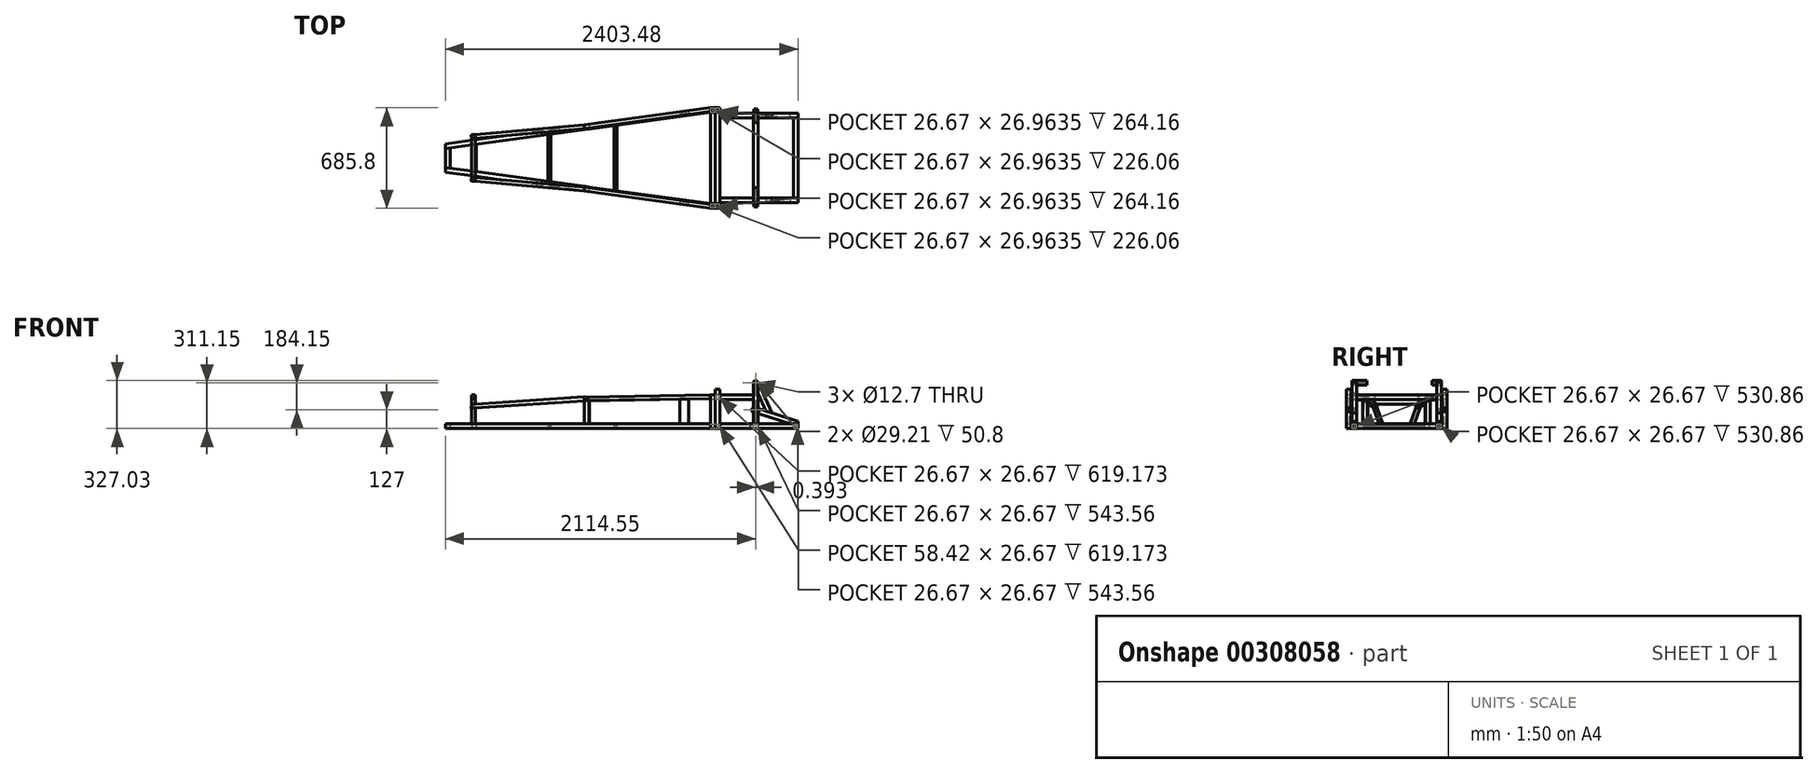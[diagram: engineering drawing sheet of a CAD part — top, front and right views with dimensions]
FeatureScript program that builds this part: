
annotation { "Feature Type Name" : "Feature", "Feature Type Description" : "" }
export const myFeature = defineFeature(function(context is Context, id is Id, definition is map)
    precondition{}
    {
        {
            var Q0;
            Q0=qCreatedBy(makeId("Top.planeOp"),FACE);
            var sketch = newSketch(context, id + "F0", { "sketchPlane" : qUnion([Q0])});
            skLineSegment(sketch, "E0.left", {"start": v(1201.74, -304.8) * mm, "end": v(1201.74, 304.8) * mm});
            skPoint(sketch, "E0.middle", {"position": v(0, 0) * mm});
            skLineSegment(sketch, "E1.0", {"start": v(636.59, -342.9) * mm, "end": v(636.59, -310.86) * mm});
            skLineSegment(sketch, "E2.0", {"start": v(668.34, -342.9) * mm, "end": v(668.34, 342.9) * mm});
            skLineSegment(sketch, "E3", {"start": v(604.84, 342.9) * mm, "end": v(604.84, -342.9) * mm});
            skLineSegment(sketch, "E4", {"start": v(604.84, 342.9) * mm, "end": v(668.34, 342.9) * mm});
            skLineSegment(sketch, "E5.trimOffspring", {"start": v(-1169.99, 0) * mm, "end": v(-1023.94, 0) * mm, "construction": true});
            skLineSegment(sketch, "E6.trimOffspring", {"start": v(668.34, 0) * mm, "end": v(1201.74, 0) * mm, "construction": true});
            skLineSegment(sketch, "E7", {"start": v(604.84, -342.9) * mm, "end": v(668.34, -342.9) * mm});
            skLineSegment(sketch, "E8.0", {"start": v(668.34, -304.8) * mm, "end": v(1201.74, -304.8) * mm});
            skLineSegment(sketch, "E9.0", {"start": v(668.34, 304.8) * mm, "end": v(1201.74, 304.8) * mm});
            skLineSegment(sketch, "E10.0", {"start": v(668.34, 273.05) * mm, "end": v(1201.74, 273.05) * mm});
            skLineSegment(sketch, "E11.0", {"start": v(668.34, -273.05) * mm, "end": v(1201.74, -273.05) * mm});
            skLineSegment(sketch, "E12.0", {"start": v(1169.99, -273.05) * mm, "end": v(1169.99, 273.05) * mm});
            skLineSegment(sketch, "E13.0", {"start": v(-1169.99, -68.98) * mm, "end": v(-1169.99, 68.98) * mm});
            skLineSegment(sketch, "E14", {"start": v(-1023.94, 0) * mm, "end": v(604.84, 0) * mm, "construction": true});
            skLineSegment(sketch, "E15", {"start": v(-1023.94, -88.89) * mm, "end": v(-1023.94, 88.89) * mm});
            skLineSegment(sketch, "E16", {"start": v(604.84, 342.9) * mm, "end": v(-1201.74, 96.7) * mm});
            skLineSegment(sketch, "E17", {"start": v(-1201.74, -96.7) * mm, "end": v(-1201.74, -64.66) * mm});
            skLineSegment(sketch, "E18.0", {"start": v(604.84, 310.86) * mm, "end": v(-1201.74, 64.66) * mm});
            skLineSegment(sketch, "E19.MirrorCS", {"start": v(604.84, -310.86) * mm, "end": v(-1201.74, -64.66) * mm});
            skLineSegment(sketch, "E20.MirrorCS", {"start": v(604.84, -342.9) * mm, "end": v(-1201.74, -96.7) * mm});
            skLineSegment(sketch, "E21.0", {"start": v(-992.19, -93.21) * mm, "end": v(-992.19, 93.21) * mm});
            skLineSegment(sketch, "E22.trimOffspring", {"start": v(-1201.74, 64.66) * mm, "end": v(-1201.74, 96.7) * mm});
            skLineSegment(sketch, "E23", {"start": v(-1201.74, -64.66) * mm, "end": v(-1201.74, 64.66) * mm});
            skLineSegment(sketch, "E24.0", {"start": v(-503.24, -159.85) * mm, "end": v(-503.24, 159.85) * mm});
            skLineSegment(sketch, "E25.0", {"start": v(-484.19, -162.44) * mm, "end": v(-484.19, 162.44) * mm});
            skLineSegment(sketch, "E26", {"start": v(604.84, -310.86) * mm, "end": v(668.34, -310.86) * mm});
            skLineSegment(sketch, "E27", {"start": v(604.84, 310.86) * mm, "end": v(668.34, 310.86) * mm});
            skLineSegment(sketch, "E28", {"start": v(636.59, 310.86) * mm, "end": v(636.59, 342.9) * mm});
            skSolve(sketch);
        }
        {
            var Q0;
            {var subQ5=sQuery(id+"F0.wireOp",EDGE,"E16");Q0=makeQuery(id+"F0.imprint","IMPRINT",FACE,{"disambiguationData":[TD([[makeQuery(id+"F0.imprint","IMPRINT",EDGE,{"derivedFrom":subQ5}),1.0]])]});}
            var Q1;
            {var subQ6=sQuery(id+"F0.wireOp",EDGE,"E17");Q1=makeQuery(id+"F0.imprint","IMPRINT",FACE,{"disambiguationData":[TD([[makeQuery(id+"F0.imprint","IMPRINT",EDGE,{"derivedFrom":subQ6}),-1.0]])]});}
            extrude(context, id + "F1", {"entities" : qUnion([Q0, Q1]), "depth" : 31.75 * mm});
        }
        {
            var Q0;
            {var subQ0=sQuery(id+"F0.wireOp",EDGE,"E15");Q0=makeQuery(id+"F0.imprint","IMPRINT",FACE,{"disambiguationData":[TD([[makeQuery(id+"F0.imprint","IMPRINT",EDGE,{"derivedFrom":subQ0}),-1.0]])]});}
            var Q1;
            {var subQ0=sQuery(id+"F0.wireOp",EDGE,"E13.0");Q1=makeQuery(id+"F0.imprint","IMPRINT",FACE,{"disambiguationData":[TD([[makeQuery(id+"F0.imprint","IMPRINT",EDGE,{"derivedFrom":subQ0}),1.0]])]});}
            extrude(context, id + "F2", {"entities" : qUnion([Q0, Q1]), "depth" : 31.75 * mm});
        }
        {
            var Q0;
            {var subQ0=sQuery(id+"F0.wireOp",EDGE,"E24.0");Q0=makeQuery(id+"F0.imprint","IMPRINT",FACE,{"disambiguationData":[TD([[makeQuery(id+"F0.imprint","IMPRINT",EDGE,{"derivedFrom":subQ0}),-1.0]])]});}
            extrude(context, id + "F3", {"entities" : qUnion([Q0]), "depth" : 19.05 * mm});
        }
        {
            var Q0;
            {var subQ0=sQuery(id+"F0.wireOp",EDGE,"E2.0");var subQ4=makeQuery(id+"F0.imprint","INTERSECT",VERTEX,{"derivedFrom":[subQ0,sQuery(id+"F0.wireOp",EDGE,"E8.0")]});Q0=makeQuery(id+"F0.imprint","IMPRINT",FACE,{"disambiguationData":[TD([[makeQuery(id+"F0.imprint","IMPRINT",EDGE,{"disambiguationData":[TD([[subQ4,1.0]])],"derivedFrom":subQ0}),1.0]])]});}
            extrude(context, id + "F4", {"entities" : qUnion([Q0]), "depth" : 31.75 * mm});
        }
        {
            var Q0;
            {var subQ5=sQuery(id+"F0.wireOp",EDGE,"E28");Q0=makeQuery(id+"F0.imprint","IMPRINT",FACE,{"disambiguationData":[TD([[makeQuery(id+"F0.imprint","IMPRINT",EDGE,{"derivedFrom":subQ5}),1.0]])]});}
            extrude(context, id + "F5", {"entities" : qUnion([Q0]), "depth" : 228.6 * mm});
        }
        {
            var Q0;
            {var subQ0=sQuery(id+"F0.wireOp",EDGE,"E1.0");Q0=makeQuery(id+"F0.imprint","IMPRINT",FACE,{"disambiguationData":[TD([[makeQuery(id+"F0.imprint","IMPRINT",EDGE,{"derivedFrom":subQ0}),1.0]])]});}
            extrude(context, id + "F6", {"entities" : qUnion([Q0]), "depth" : 228.6 * mm});
        }
        {
            var Q0;
            {var subQ5=sQuery(id+"F0.wireOp",EDGE,"E28");Q0=makeQuery(id+"F0.imprint","IMPRINT",FACE,{"disambiguationData":[TD([[makeQuery(id+"F0.imprint","IMPRINT",EDGE,{"derivedFrom":subQ5}),-1.0]])]});}
            extrude(context, id + "F7", {"entities" : qUnion([Q0]), "depth" : 266.7 * mm});
        }
        {
            var Q0;
            {var subQ0=sQuery(id+"F0.wireOp",EDGE,"E1.0");Q0=makeQuery(id+"F0.imprint","IMPRINT",FACE,{"disambiguationData":[TD([[makeQuery(id+"F0.imprint","IMPRINT",EDGE,{"derivedFrom":subQ0}),-1.0]])]});}
            extrude(context, id + "F8", {"entities" : qUnion([Q0]), "depth" : 266.7 * mm});
        }
        {
            var Q0;
            {var subQ5=sQuery(id+"F0.wireOp",EDGE,"E12.0");Q0=makeQuery(id+"F0.imprint","IMPRINT",FACE,{"disambiguationData":[TD([[makeQuery(id+"F0.imprint","IMPRINT",EDGE,{"derivedFrom":subQ5}),-1.0]])]});}
            extrude(context, id + "F9", {"entities" : qUnion([Q0]), "depth" : 31.75 * mm});
        }
        {
            var Q0;
            {var subQ4=sQuery(id+"F0.wireOp",EDGE,"E9.0");Q0=makeQuery(id+"F0.imprint","IMPRINT",FACE,{"disambiguationData":[TD([[makeQuery(id+"F0.imprint","IMPRINT",EDGE,{"derivedFrom":subQ4}),-1.0]])]});}
            var Q1;
            {var subQ4=sQuery(id+"F0.wireOp",EDGE,"E8.0");Q1=makeQuery(id+"F0.imprint","IMPRINT",FACE,{"disambiguationData":[TD([[makeQuery(id+"F0.imprint","IMPRINT",EDGE,{"derivedFrom":subQ4}),1.0]])]});}
            extrude(context, id + "F10", {"entities" : qUnion([Q0, Q1]), "depth" : 31.75 * mm});
        }
        {
            var Q0;
            {var subQ0=sQuery(id+"F0.wireOp",EDGE,"E19.MirrorCS");Q0=makeQuery(id+"F2.opExtrude","SWEPT_FACE",FACE,{"disambiguationData":[OSD([subQ0]),TDD([makeQuery(id+"F0.imprint","IMPRINT",EDGE,{"disambiguationData":[TD([[makeQuery(id+"F0.imprint","INTERSECT",VERTEX,{"derivedFrom":[sQuery(id+"F0.wireOp",EDGE,"E13.0"),subQ0]}),-1.0]])],"derivedFrom":subQ0})])]});}
            var Q1;
            {var subQ0=sQuery(id+"F0.wireOp",EDGE,"E19.MirrorCS");Q1=makeQuery(id+"F2.opExtrude","SWEPT_FACE",FACE,{"disambiguationData":[OSD([subQ0]),TDD([makeQuery(id+"F0.imprint","IMPRINT",EDGE,{"disambiguationData":[TD([[makeQuery(id+"F0.imprint","INTERSECT",VERTEX,{"derivedFrom":[sQuery(id+"F0.wireOp",EDGE,"E15"),subQ0]}),1.0]])],"derivedFrom":subQ0})])]});}
            var Q2;
            Q2=makeQuery(id+"F3.opExtrude","SWEPT_FACE",FACE,{"disambiguationData":[OSD([sQuery(id+"F0.wireOp",EDGE,"E19.MirrorCS")])]});
            shell(context, id + "F11", {"entities" : qUnion([Q0, Q1, Q2]), "thickness" : 2.54 * mm});
        }
        {
            var Q0;
            Q0=makeQuery(id+"F1.opExtrude","SWEPT_FACE",FACE,{"disambiguationData":[OSD([sQuery(id+"F0.wireOp",EDGE,"E22.trimOffspring")])]});
            var Q1;
            Q1=makeQuery(id+"F1.opExtrude","SWEPT_FACE",FACE,{"disambiguationData":[OSD([sQuery(id+"F0.wireOp",EDGE,"E17")])]});
            var Q2;
            Q2=makeQuery(id+"F6.opExtrude","CAP_FACE",FACE,{"disambiguationData":[OSD([sQuery(id+"F0.wireOp",EDGE,"E1.0"),sQuery(id+"F0.wireOp",EDGE,"E3"),sQuery(id+"F0.wireOp",EDGE,"E7"),sQuery(id+"F0.wireOp",EDGE,"E26")])],"isStart":false});
            var Q3;
            Q3=makeQuery(id+"F8.opExtrude","CAP_FACE",FACE,{"disambiguationData":[OSD([sQuery(id+"F0.wireOp",EDGE,"E1.0"),sQuery(id+"F0.wireOp",EDGE,"E2.0"),sQuery(id+"F0.wireOp",EDGE,"E7"),sQuery(id+"F0.wireOp",EDGE,"E26")])],"isStart":false});
            var Q4;
            Q4=makeQuery(id+"F5.opExtrude","CAP_FACE",FACE,{"disambiguationData":[OSD([sQuery(id+"F0.wireOp",EDGE,"E3"),sQuery(id+"F0.wireOp",EDGE,"E4"),sQuery(id+"F0.wireOp",EDGE,"E27"),sQuery(id+"F0.wireOp",EDGE,"E28")])],"isStart":false});
            var Q5;
            Q5=makeQuery(id+"F7.opExtrude","CAP_FACE",FACE,{"disambiguationData":[OSD([sQuery(id+"F0.wireOp",EDGE,"E2.0"),sQuery(id+"F0.wireOp",EDGE,"E4"),sQuery(id+"F0.wireOp",EDGE,"E27"),sQuery(id+"F0.wireOp",EDGE,"E28")])],"isStart":false});
            var Q6;
            {var subQ0=sQuery(id+"F0.wireOp",EDGE,"E0.left");Q6=makeQuery(id+"F10.opExtrude","SWEPT_FACE",FACE,{"disambiguationData":[OSD([subQ0]),TDD([makeQuery(id+"F0.imprint","IMPRINT",EDGE,{"disambiguationData":[TD([[makeQuery(id+"F0.imprint","INTERSECT",VERTEX,{"derivedFrom":[subQ0,sQuery(id+"F0.wireOp",EDGE,"E8.0")]}),-1.0]])],"derivedFrom":subQ0})])]});}
            var Q7;
            {var subQ0=sQuery(id+"F0.wireOp",EDGE,"E0.left");Q7=makeQuery(id+"F10.opExtrude","SWEPT_FACE",FACE,{"disambiguationData":[OSD([subQ0]),TDD([makeQuery(id+"F0.imprint","IMPRINT",EDGE,{"disambiguationData":[TD([[makeQuery(id+"F0.imprint","INTERSECT",VERTEX,{"derivedFrom":[subQ0,sQuery(id+"F0.wireOp",EDGE,"E9.0")]}),1.0]])],"derivedFrom":subQ0})])]});}
            shell(context, id + "F12", {"entities" : qUnion([Q0, Q1, Q2, Q3, Q4, Q5, Q6, Q7]), "thickness" : 2.54 * mm});
        }
        {
            var Q0;
            Q0=makeQuery(id+"F4.opExtrude","SWEPT_FACE",FACE,{"disambiguationData":[OSD([sQuery(id+"F0.wireOp",EDGE,"E26")])]});
            shell(context, id + "F13", {"entities" : qUnion([Q0]), "thickness" : 2.54 * mm});
        }
        {
            var Q0;
            Q0=makeQuery(id+"F9.opExtrude","SWEPT_FACE",FACE,{"disambiguationData":[OSD([sQuery(id+"F0.wireOp",EDGE,"E11.0")])]});
            shell(context, id + "F14", {"entities" : qUnion([Q0]), "thickness" : 2.54 * mm});
        }
        {
            var Q0;
            Q0=makeQuery(id+"F5.opExtrude","SWEPT_FACE",FACE,{"disambiguationData":[OSD([sQuery(id+"F0.wireOp",EDGE,"E27")])]});
            var sketch = newSketch(context, id + "F15", { "sketchPlane" : qUnion([Q0])});
            skLineSegment(sketch, "E29.bottom", {"start": v(604.84, 228.6) * mm, "end": v(636.59, 228.6) * mm});
            skLineSegment(sketch, "E29.top", {"start": v(604.84, 196.85) * mm, "end": v(636.59, 196.85) * mm});
            skLineSegment(sketch, "E29.left", {"start": v(604.84, 228.6) * mm, "end": v(604.84, 196.85) * mm});
            skLineSegment(sketch, "E29.right", {"start": v(636.59, 228.6) * mm, "end": v(636.59, 196.85) * mm});
            skSolve(sketch);
        }
        {
            var Q0;
            Q0 = qSketchRegion(id + "F15", true);
            extrude(context, id + "F16", {"entities" : qUnion([Q0]), "endBound" : BoundingType.UP_TO_NEXT, "depth" : 25.4 * mm});
        }
        {
            var Q0;
            Q0=makeQuery(id+"F7.opExtrude","SWEPT_FACE",FACE,{"disambiguationData":[OSD([sQuery(id+"F0.wireOp",EDGE,"E27")])]});
            var sketch = newSketch(context, id + "F17", { "sketchPlane" : qUnion([Q0])});
            skLineSegment(sketch, "E30.bottom", {"start": v(636.59, 228.6) * mm, "end": v(668.34, 228.6) * mm});
            skLineSegment(sketch, "E30.top", {"start": v(636.59, 196.85) * mm, "end": v(668.34, 196.85) * mm});
            skLineSegment(sketch, "E30.left", {"start": v(636.59, 228.6) * mm, "end": v(636.59, 196.85) * mm});
            skLineSegment(sketch, "E30.right", {"start": v(668.34, 228.6) * mm, "end": v(668.34, 196.85) * mm});
            skSolve(sketch);
        }
        {
            var Q0;
            Q0 = qSketchRegion(id + "F17", true);
            extrude(context, id + "F18", {"entities" : qUnion([Q0]), "endBound" : BoundingType.UP_TO_NEXT, "depth" : 25.4 * mm});
        }
        {
            var Q0;
            Q0=makeQuery(id+"F18.opExtrude","CAP_FACE",FACE,{"disambiguationData":[OSD([sQuery(id+"F17.wireOp",EDGE,"E30.bottom"),sQuery(id+"F17.wireOp",EDGE,"E30.top"),sQuery(id+"F17.wireOp",EDGE,"E30.left"),sQuery(id+"F17.wireOp",EDGE,"E30.right")])],"isStart":false});
            shell(context, id + "F19", {"entities" : qUnion([Q0]), "thickness" : 2.54 * mm});
        }
        {
            var Q0;
            Q0=makeQuery(id+"F10.opExtrude","CAP_FACE",FACE,{"disambiguationData":[OSD([sQuery(id+"F0.wireOp",EDGE,"E0.left"),sQuery(id+"F0.wireOp",EDGE,"E2.0"),sQuery(id+"F0.wireOp",EDGE,"E8.0"),sQuery(id+"F0.wireOp",EDGE,"E11.0")])],"isStart":false});
            var sketch = newSketch(context, id + "F20", { "sketchPlane" : qUnion([Q0])});
            skLineSegment(sketch, "E31.bottom", {"start": v(896.94, -273.05) * mm, "end": v(928.69, -273.05) * mm});
            skLineSegment(sketch, "E31.top", {"start": v(896.94, -304.8) * mm, "end": v(928.69, -304.8) * mm});
            skLineSegment(sketch, "E31.left", {"start": v(896.94, -273.05) * mm, "end": v(896.94, -304.8) * mm});
            skLineSegment(sketch, "E31.right", {"start": v(928.69, -273.05) * mm, "end": v(928.69, -304.8) * mm});
            skSolve(sketch);
        }
        {
            var Q0;
            Q0 = qSketchRegion(id + "F20", true);
            extrude(context, id + "F21", {"entities" : qUnion([Q0]), "depth" : 279.4 * mm});
        }
        {
            var Q0;
            Q0=makeQuery(id+"F21.opExtrude","SWEPT_FACE",FACE,{"disambiguationData":[OSD([sQuery(id+"F20.wireOp",EDGE,"E31.left")])]});
            var sketch = newSketch(context, id + "F22", { "sketchPlane" : qUnion([Q0])});
            skLineSegment(sketch, "E32.bottom", {"start": v(273.05, 228.6) * mm, "end": v(304.8, 228.6) * mm});
            skLineSegment(sketch, "E32.top", {"start": v(273.05, 196.85) * mm, "end": v(304.8, 196.85) * mm});
            skLineSegment(sketch, "E32.left", {"start": v(273.05, 228.6) * mm, "end": v(273.05, 196.85) * mm});
            skLineSegment(sketch, "E32.right", {"start": v(304.8, 228.6) * mm, "end": v(304.8, 196.85) * mm});
            skSolve(sketch);
        }
        {
            var Q0;
            Q0 = qSketchRegion(id + "F22", true);
            extrude(context, id + "F23", {"entities" : qUnion([Q0]), "endBound" : BoundingType.UP_TO_NEXT, "depth" : 25.4 * mm});
        }
        {
            var Q0;
            Q0=makeQuery(id+"F21.opExtrude","SWEPT_FACE",FACE,{"disambiguationData":[OSD([sQuery(id+"F20.wireOp",EDGE,"E31.top")])]});
            var sketch = newSketch(context, id + "F24", { "sketchPlane" : qUnion([Q0])});
            skLineSegment(sketch, "E33", {"start": v(896.94, 311.15) * mm, "end": v(928.69, 311.15) * mm});
            skCircle(sketch, "E34", {"center": v(912.81, 311.15) * mm, "radius": 15.88 * mm});
            skSolve(sketch);
        }
        {
            var Q0;
            Q0 = qSketchRegion(id + "F24", true);
            extrude(context, id + "F25", {"entities" : qUnion([Q0]), "operationType" : NewBodyOperationType.REMOVE, "oppositeDirection" : true, "depth" : 31.75 * mm});
        }
        {
            var Q0;
            Q0=makeQuery(id+"F21.opExtrude","SWEPT_FACE",FACE,{"disambiguationData":[OSD([sQuery(id+"F20.wireOp",EDGE,"E31.top")])]});
            var sketch = newSketch(context, id + "F26", { "sketchPlane" : qUnion([Q0])});
            skLineSegment(sketch, "E35", {"start": v(896.94, 311.15) * mm, "end": v(928.69, 311.15) * mm});
            skCircle(sketch, "E36", {"center": v(912.81, 311.15) * mm, "radius": 15.88 * mm});
            skSolve(sketch);
        }
        {
            var Q0;
            Q0 = qSketchRegion(id + "F26", true);
            extrude(context, id + "F27", {"entities" : qUnion([Q0]), "oppositeDirection" : true, "depth" : 101.6 * mm});
        }
        {
            var Q0;
            Q0=makeQuery(id+"F27.opExtrude","CAP_FACE",FACE,{"disambiguationData":[OSD([sQuery(id+"F26.wireOp",EDGE,"E36")])],"isStart":true});
            var sketch = newSketch(context, id + "F28", { "sketchPlane" : qUnion([Q0])});
            skCircle(sketch, "E37", {"center": v(912.81, 311.15) * mm, "radius": 14.6 * mm});
            skSolve(sketch);
        }
        {
            var Q0;
            Q0 = qSketchRegion(id + "F28", true);
            extrude(context, id + "F29", {"entities" : qUnion([Q0]), "operationType" : NewBodyOperationType.REMOVE, "oppositeDirection" : true, "depth" : 50.8 * mm});
        }
        {
            var Q0;
            Q0=makeQuery(id+"F29.boolean.opBoolean","COPY",FACE,{"derivedFrom":makeQuery(id+"F29.opExtrude","CAP_FACE",FACE,{"disambiguationData":[OSD([sQuery(id+"F28.wireOp",EDGE,"E37")])],"isStart":false})});
            var sketch = newSketch(context, id + "F30", { "sketchPlane" : qUnion([Q0])});
            skCircle(sketch, "E38", {"center": v(912.81, 311.15) * mm, "radius": 4.95 * mm});
            skSolve(sketch);
        }
        {
            var Q0;
            Q0 = qSketchRegion(id + "F30", true);
            extrude(context, id + "F31", {"entities" : qUnion([Q0]), "operationType" : NewBodyOperationType.REMOVE, "endBound" : BoundingType.THROUGH_ALL, "oppositeDirection" : true, "depth" : 25.4 * mm});
        }
        {
            var Q0;
            Q0=makeQuery(id+"F23.opExtrude","SWEPT_BODY",BODY,{"disambiguationData":[OSD([sQuery(id+"F22.wireOp",EDGE,"E32.bottom"),sQuery(id+"F22.wireOp",EDGE,"E32.top"),sQuery(id+"F22.wireOp",EDGE,"E32.left"),sQuery(id+"F22.wireOp",EDGE,"E32.right")])]});
            var Q1;
            Q1=makeQuery(id+"F21.opExtrude","SWEPT_BODY",BODY,{"disambiguationData":[OSD([sQuery(id+"F20.wireOp",EDGE,"E31.bottom"),sQuery(id+"F20.wireOp",EDGE,"E31.top"),sQuery(id+"F20.wireOp",EDGE,"E31.left"),sQuery(id+"F20.wireOp",EDGE,"E31.right")])]});
            var Q2;
            Q2=makeQuery(id+"F27.opExtrude","SWEPT_BODY",BODY,{"disambiguationData":[OSD([sQuery(id+"F26.wireOp",EDGE,"E36")])]});
            var Q3;
            Q3=qCreatedBy(makeId("Front.planeOp"),FACE);
            mirror(context, id + "F32", {"entities" : qUnion([Q0, Q1, Q2]), "mirrorPlane" : qUnion([Q3])});
        }
        {
            var Q0;
            Q0=makeQuery(id+"F23.opExtrude","SWEPT_FACE",FACE,{"disambiguationData":[OSD([sQuery(id+"F22.wireOp",EDGE,"E32.right")])]});
            var sketch = newSketch(context, id + "F33", { "sketchPlane" : qUnion([Q0])});
            skLineSegment(sketch, "E39", {"start": v(897.33, 127) * mm, "end": v(929.08, 127) * mm});
            skCircle(sketch, "E40", {"center": v(913.2, 127) * mm, "radius": 25.4 * mm});
            skSolve(sketch);
        }
        {
            var Q0;
            Q0 = qSketchRegion(id + "F33", true);
            extrude(context, id + "F34", {"entities" : qUnion([Q0]), "depth" : 3.17 * mm});
        }
        {
            var Q0;
            Q0=makeQuery(id+"F34.opExtrude","CAP_FACE",FACE,{"disambiguationData":[OSD([sQuery(id+"F33.wireOp",EDGE,"E40")])],"isStart":false});
            var sketch = newSketch(context, id + "F35", { "sketchPlane" : qUnion([Q0])});
            skCircle(sketch, "E41", {"center": v(913.2, 127) * mm, "radius": 12.7 * mm});
            skSolve(sketch);
        }
        {
            var Q0;
            Q0=makeQuery(id+"F35.imprint","IMPRINT",FACE,{"disambiguationData":[TD([[makeQuery(id+"F35.imprint","IMPRINT",EDGE,{"derivedFrom":sQuery(id+"F35.wireOp",EDGE,"E41")}),1.0]])]});
            extrude(context, id + "F36", {"entities" : qUnion([Q0]), "depth" : 25.4 * mm});
        }
        {
            var Q0;
            Q0=makeQuery(id+"F36.opExtrude","CAP_FACE",FACE,{"disambiguationData":[OSD([sQuery(id+"F35.wireOp",EDGE,"E41")])],"isStart":false});
            var sketch = newSketch(context, id + "F37", { "sketchPlane" : qUnion([Q0])});
            skCircle(sketch, "E42", {"center": v(913.2, 127) * mm, "radius": 6.35 * mm});
            skSolve(sketch);
        }
        {
            var Q0;
            Q0 = qSketchRegion(id + "F37", true);
            extrude(context, id + "F38", {"entities" : qUnion([Q0]), "operationType" : NewBodyOperationType.REMOVE, "endBound" : BoundingType.THROUGH_ALL, "oppositeDirection" : true, "depth" : 85.72 * mm});
        }
        {
            var Q0;
            Q0=makeQuery(id+"F34.opExtrude","SWEPT_BODY",BODY,{"disambiguationData":[OSD([sQuery(id+"F33.wireOp",EDGE,"E40")])]});
            var Q1;
            Q1=makeQuery(id+"F36.opExtrude","SWEPT_BODY",BODY,{"disambiguationData":[OSD([sQuery(id+"F35.wireOp",EDGE,"E41")])]});
            var Q2;
            Q2=qCreatedBy(makeId("Front.planeOp"),FACE);
            mirror(context, id + "F39", {"operationType" : NewBodyOperationType.ADD, "entities" : qUnion([Q0, Q1]), "mirrorPlane" : qUnion([Q2])});
        }
        {
            var Q0;
            Q0=makeQuery(id+"F21.opExtrude","SWEPT_FACE",FACE,{"disambiguationData":[OSD([sQuery(id+"F20.wireOp",EDGE,"E31.top")])]});
            var sketch = newSketch(context, id + "F40", { "sketchPlane" : qUnion([Q0])});
            skLineSegment(sketch, "E43", {"start": v(1200.59, 32.3) * mm, "end": v(1201.67, 31.96) * mm});
            skLineSegment(sketch, "E44.0", {"start": v(928.69, 136.04) * mm, "end": v(1201.67, 48.62) * mm});
            skLineSegment(sketch, "E45.0", {"start": v(928.69, 102.7) * mm, "end": v(1148.53, 32.3) * mm});
            skLineSegment(sketch, "E46", {"start": v(928.69, 102.7) * mm, "end": v(928.69, 136.04) * mm});
            skLineSegment(sketch, "E47", {"start": v(1148.53, 32.3) * mm, "end": v(1201.67, 32.3) * mm});
            skLineSegment(sketch, "E48", {"start": v(1201.67, 31.96) * mm, "end": v(1201.67, 48.62) * mm});
            skSolve(sketch);
        }
        {
            var Q0;
            Q0=makeQuery(id+"F9.opExtrude","SWEPT_FACE",FACE,{"disambiguationData":[OSD([sQuery(id+"F0.wireOp",EDGE,"E0.left")])]});
            var sketch = newSketch(context, id + "F41", { "sketchPlane" : qUnion([Q0])});
            skLineSegment(sketch, "E49", {"start": v(-273.05, 0) * mm, "end": v(-273.05, 59.84) * mm});
            skLineSegment(sketch, "E50", {"start": v(-273.05, 59.84) * mm, "end": v(-349.24, 59.84) * mm});
            skLineSegment(sketch, "E51", {"start": v(-273.05, 0) * mm, "end": v(-342.61, 0) * mm});
            skLineSegment(sketch, "E52", {"start": v(-349.24, 59.84) * mm, "end": v(-342.61, 0) * mm});
            skSolve(sketch);
        }
        {
            var Q0;
            {var subQ1=sQuery(id+"F41.wireOp",EDGE,"E50");Q0=makeQuery(id+"F41.imprint","IMPRINT",FACE,{"disambiguationData":[TD([[makeQuery(id+"F41.imprint","IMPRINT",EDGE,{"derivedFrom":subQ1}),1.0]])]});}
            extrude(context, id + "F42", {"entities" : qUnion([Q0]), "operationType" : NewBodyOperationType.REMOVE, "depth" : 25.4 * mm});
        }
        {
            var Q0;
            Q0 = qSketchRegion(id + "F40", true);
            extrude(context, id + "F43", {"entities" : qUnion([Q0]), "oppositeDirection" : true, "depth" : 31.75 * mm});
        }
        {
            var Q0;
            Q0=makeQuery(id+"F43.opExtrude","SWEPT_FACE",FACE,{"disambiguationData":[OSD([sQuery(id+"F40.wireOp",EDGE,"E46")])]});
            shell(context, id + "F44", {"entities" : qUnion([Q0]), "thickness" : 2.54 * mm});
        }
        {
            var Q0;
            Q0=makeQuery(id+"F43.opExtrude","SWEPT_BODY",BODY,{"disambiguationData":[OSD([sQuery(id+"F40.wireOp",EDGE,"E43"),sQuery(id+"F40.wireOp",EDGE,"E44.0"),sQuery(id+"F40.wireOp",EDGE,"E45.0"),sQuery(id+"F40.wireOp",EDGE,"E46"),sQuery(id+"F40.wireOp",EDGE,"E47"),sQuery(id+"F40.wireOp",EDGE,"E48")])]});
            var Q1;
            Q1=qCreatedBy(makeId("Front.planeOp"),FACE);
            mirror(context, id + "F45", {"entities" : qUnion([Q0]), "mirrorPlane" : qUnion([Q1])});
        }
        {
            var Q0;
            Q0=makeQuery(id+"F32.opPattern","COPY",FACE,{"derivedFrom":makeQuery(id+"F21.opExtrude","SWEPT_FACE",FACE,{"disambiguationData":[OSD([sQuery(id+"F20.wireOp",EDGE,"E31.bottom")])]}),"instanceName":"1"});
            var sketch = newSketch(context, id + "F46", { "sketchPlane" : qUnion([Q0])});
            skLineSegment(sketch, "E53", {"start": v(896.94, 31.75) * mm, "end": v(896.94, 0) * mm});
            skLineSegment(sketch, "E54", {"start": v(896.94, 0) * mm, "end": v(928.69, 0) * mm});
            skLineSegment(sketch, "E55", {"start": v(928.69, 0) * mm, "end": v(928.69, 31.75) * mm});
            skLineSegment(sketch, "E56", {"start": v(928.69, 31.75) * mm, "end": v(896.94, 31.75) * mm});
            skSolve(sketch);
        }
        {
            var Q0;
            Q0 = qSketchRegion(id + "F46", true);
            extrude(context, id + "F47", {"entities" : qUnion([Q0]), "endBound" : BoundingType.UP_TO_NEXT, "depth" : 25.4 * mm});
        }
        {
            var Q0;
            Q0=makeQuery(id+"F47.opExtrude","CAP_FACE",FACE,{"disambiguationData":[OSD([sQuery(id+"F46.wireOp",EDGE,"E53"),sQuery(id+"F46.wireOp",EDGE,"E54"),sQuery(id+"F46.wireOp",EDGE,"E55"),sQuery(id+"F46.wireOp",EDGE,"E56")])],"isStart":false});
            shell(context, id + "F48", {"entities" : qUnion([Q0]), "thickness" : 2.54 * mm});
        }
        {
            var Q0;
            Q0=makeQuery(id+"F32.opPattern","COPY",BODY,{"derivedFrom":makeQuery(id+"F27.opExtrude","SWEPT_BODY",BODY,{"disambiguationData":[OSD([sQuery(id+"F26.wireOp",EDGE,"E36")])]}),"instanceName":"1"});
            deleteBodies(context, id + "F49", {"entities" : qUnion([Q0])});
        }
        {
            var Q0;
            Q0=makeQuery(id+"F39.boolean.opBoolean","SPLIT",FACE,{"disambiguationData":[TD([makeQuery(id+"F32.opPattern","COPY",FACE,{"derivedFrom":makeQuery(id+"F25.boolean.opBoolean","COPY",FACE,{"derivedFrom":makeQuery(id+"F25.opExtrude","SWEPT_FACE",FACE,{"disambiguationData":[OSD([sQuery(id+"F24.wireOp",EDGE,"E34")])]})}),"instanceName":"1"})])],"derivedFrom":makeQuery(id+"F32.opPattern","COPY",FACE,{"derivedFrom":makeQuery(id+"F21.opExtrude","SWEPT_FACE",FACE,{"disambiguationData":[OSD([sQuery(id+"F20.wireOp",EDGE,"E31.top")])]}),"instanceName":"1"})});
            var sketch = newSketch(context, id + "F50", { "sketchPlane" : qUnion([Q0])});
            skLineSegment(sketch, "E57", {"start": v(-928.69, 311.15) * mm, "end": v(-896.94, 311.15) * mm});
            skCircle(sketch, "E58", {"center": v(-912.81, 311.15) * mm, "radius": 15.75 * mm});
            skCircle(sketch, "E59", {"center": v(-912.81, 311.15) * mm, "radius": 6.35 * mm});
            skSolve(sketch);
        }
        {
            var Q0;
            Q0 = qSketchRegion(id + "F50", true);
            var Q1;
            {var subQ0=sQuery(id+"F50.wireOp",EDGE,"E58");var subQ1=sQuery(id+"F50.wireOp",EDGE,"E57");var subQ2=makeQuery(id+"F50.imprint","INTERSECT",VERTEX,{"disambiguationData":[OD(0.0)],"derivedFrom":[subQ1,subQ0]});Q1=makeQuery(id+"F50.imprint","IMPRINT",FACE,{"disambiguationData":[TD([[makeQuery(id+"F50.imprint","IMPRINT",EDGE,{"disambiguationData":[TD([[subQ2,-1.0]])],"derivedFrom":subQ1}),1.0]])]});}
            extrude(context, id + "F51", {"entities" : qUnion([Q0, Q1]), "oppositeDirection" : true, "depth" : 63.5 * mm});
        }
        {
            var Q0;
            Q0 = qSketchRegion(id + "F50", true);
            extrude(context, id + "F52", {"entities" : qUnion([Q0]), "operationType" : NewBodyOperationType.ADD, "oppositeDirection" : true, "depth" : 63.5 * mm});
        }
        {
            var Q0;
            Q0=makeQuery(id+"F51.opExtrude","CAP_FACE",FACE,{"disambiguationData":[OSD([sQuery(id+"F50.wireOp",EDGE,"E58"),sQuery(id+"F50.wireOp",EDGE,"E59")])],"isStart":true});
            var sketch = newSketch(context, id + "F53", { "sketchPlane" : qUnion([Q0])});
            skCircle(sketch, "E60", {"center": v(-912.81, 311.15) * mm, "radius": 14.6 * mm});
            skCircle(sketch, "E61", {"center": v(-912.81, 311.15) * mm, "radius": 6.35 * mm});
            skSolve(sketch);
        }
        {
            var Q0;
            Q0 = qSketchRegion(id + "F53", true);
            extrude(context, id + "F54", {"entities" : qUnion([Q0]), "operationType" : NewBodyOperationType.REMOVE, "oppositeDirection" : true, "depth" : 50.8 * mm});
        }
        {
            var Q0;
            Q0=makeQuery(id+"F1.opExtrude","CAP_FACE",FACE,{"disambiguationData":[OSD([sQuery(id+"F0.wireOp",EDGE,"E3"),sQuery(id+"F0.wireOp",EDGE,"E17"),sQuery(id+"F0.wireOp",EDGE,"E19.MirrorCS"),sQuery(id+"F0.wireOp",EDGE,"E20.MirrorCS")])],"isStart":false});
            var sketch = newSketch(context, id + "F55", { "sketchPlane" : qUnion([Q0])});
            skLineSegment(sketch, "E62", {"start": v(455.4, -322.54) * mm, "end": v(396.78, -314.55) * mm});
            skLineSegment(sketch, "E63", {"start": v(455.4, -322.54) * mm, "end": v(457.55, -306.8) * mm});
            skLineSegment(sketch, "E64", {"start": v(396.78, -314.55) * mm, "end": v(398.93, -298.82) * mm});
            skLineSegment(sketch, "E65.0", {"start": v(457.55, -306.8) * mm, "end": v(398.93, -298.82) * mm});
            skLineSegment(sketch, "E66.0", {"start": v(-224.11, -229.93) * mm, "end": v(-219.83, -198.47) * mm});
            skLineSegment(sketch, "E67.0", {"start": v(-255.57, -225.64) * mm, "end": v(-251.28, -194.18) * mm});
            skLineSegment(sketch, "E68", {"start": v(-255.57, -225.64) * mm, "end": v(-224.11, -229.93) * mm});
            skLineSegment(sketch, "E69.0", {"start": v(-251.28, -194.18) * mm, "end": v(-219.83, -198.47) * mm});
            skSolve(sketch);
        }
        {
            var Q0;
            Q0=makeQuery(id+"F2.opExtrude","SWEPT_FACE",FACE,{"disambiguationData":[OSD([sQuery(id+"F0.wireOp",EDGE,"E15")])]});
            var sketch = newSketch(context, id + "F56", { "sketchPlane" : qUnion([Q0])});
            skLineSegment(sketch, "E70", {"start": v(-120.93, 31.75) * mm, "end": v(120.62, 31.75) * mm});
            skLineSegment(sketch, "E71.0", {"start": v(-133.35, 228.6) * mm, "end": v(133.35, 228.6) * mm});
            skLineSegment(sketch, "E72", {"start": v(0, 139.7) * mm, "end": v(0, 416.46) * mm, "construction": true});
            skPoint(sketch, "E72.endSnap0", {"position": v(0, 31.75) * mm});
            skLineSegment(sketch, "E73.0", {"start": v(158.75, 139.7) * mm, "end": v(158.75, 203.2) * mm});
            skLineSegment(sketch, "E74.0", {"start": v(-158.75, 139.7) * mm, "end": v(-158.75, 203.2) * mm});
            skLineSegment(sketch, "E75.0", {"start": v(-158.75, 165.1) * mm, "end": v(158.75, 165.1) * mm});
            skLineSegment(sketch, "E76.0", {"start": v(-158.75, 139.7) * mm, "end": v(-131.84, 139.7) * mm});
            skLineSegment(sketch, "E77.0", {"start": v(-133.35, 139.7) * mm, "end": v(-133.35, 165.1) * mm});
            skLineSegment(sketch, "E78.0", {"start": v(133.35, 139.7) * mm, "end": v(133.35, 165.1) * mm});
            skLineSegment(sketch, "E79", {"start": v(-158.75, 139.7) * mm, "end": v(-120.93, 31.75) * mm});
            skLineSegment(sketch, "E80", {"start": v(158.75, 139.7) * mm, "end": v(120.62, 31.75) * mm});
            skLineSegment(sketch, "E81.trimOffspring", {"start": v(-131.84, 139.7) * mm, "end": v(-94.01, 31.75) * mm});
            skLineSegment(sketch, "E82", {"start": v(-158.75, 203.2) * mm, "end": v(-133.35, 228.6) * mm});
            skLineSegment(sketch, "E83", {"start": v(158.75, 203.2) * mm, "end": v(133.35, 228.6) * mm});
            skLineSegment(sketch, "E84.trimOffspring", {"start": v(-131.84, 139.7) * mm, "end": v(158.75, 139.7) * mm});
            skLineSegment(sketch, "E85.0", {"start": v(131.81, 139.7) * mm, "end": v(93.68, 31.75) * mm});
            skSolve(sketch);
        }
        {
            var Q0;
            {var subQ0=sQuery(id+"F56.wireOp",EDGE,"E79");Q0=makeQuery(id+"F56.imprint","IMPRINT",FACE,{"disambiguationData":[TD([[makeQuery(id+"F56.imprint","IMPRINT",EDGE,{"derivedFrom":subQ0}),1.0]])]});}
            var Q1;
            {var subQ3=sQuery(id+"F56.wireOp",EDGE,"E80");Q1=makeQuery(id+"F56.imprint","IMPRINT",FACE,{"disambiguationData":[TD([[makeQuery(id+"F56.imprint","IMPRINT",EDGE,{"derivedFrom":subQ3}),-1.0]])]});}
            var Q2;
            Q2=makeQuery(id+"F56.imprint","IMPRINT",FACE,{"disambiguationData":[TD([[makeQuery(id+"F56.imprint","IMPRINT",EDGE,{"derivedFrom":sQuery(id+"F56.wireOp",EDGE,"E71.0")}),-1.0]])]});
            extrude(context, id + "F57", {"entities" : qUnion([Q0, Q1, Q2]), "oppositeDirection" : true, "depth" : 25.4 * mm});
        }
        {
            var Q0;
            Q0 = qSketchRegion(id + "F55", true);
            extrude(context, id + "F58", {"entities" : qUnion([Q0]), "depth" : 168.27 * mm});
        }
        {
            var Q0;
            Q0=makeQuery(id+"F1.opExtrude","SWEPT_FACE",FACE,{"disambiguationData":[OSD([sQuery(id+"F0.wireOp",EDGE,"E20.MirrorCS")])]});
            var sketch = newSketch(context, id + "F59", { "sketchPlane" : qUnion([Q0])});
            skLineSegment(sketch, "E86", {"start": v(-222.23, 189.66) * mm, "end": v(642.95, 203.86) * mm});
            skLineSegment(sketch, "E87.0", {"start": v(-222.65, 215.06) * mm, "end": v(642.54, 229.25) * mm});
            skLineSegment(sketch, "E88", {"start": v(-222.23, 189.66) * mm, "end": v(-222.65, 215.06) * mm});
            skLineSegment(sketch, "E89", {"start": v(642.95, 203.86) * mm, "end": v(642.54, 229.25) * mm});
            skSolve(sketch);
        }
        {
            var Q0;
            Q0 = qSketchRegion(id + "F59", true);
            extrude(context, id + "F60", {"entities" : qUnion([Q0]), "oppositeDirection" : true, "depth" : 25.4 * mm});
        }
        {
            var Q0;
            Q0=makeQuery(id+"F60.opExtrude","CAP_VERTEX",VERTEX,{"disambiguationData":[OSD([sQuery(id+"F59.wireOp",EDGE,"E87.0"),sQuery(id+"F59.wireOp",EDGE,"E88")])],"isStart":true});
            var Q1;
            Q1=makeQuery(id+"F57.opExtrude","CAP_VERTEX",VERTEX,{"disambiguationData":[OSD([sQuery(id+"F56.wireOp",EDGE,"E73.0"),sQuery(id+"F56.wireOp",EDGE,"E80"),sQuery(id+"F56.wireOp",EDGE,"E84.trimOffspring")])],"isStart":false});
            var Q2;
            Q2=makeQuery(id+"F57.opExtrude","CAP_VERTEX",VERTEX,{"disambiguationData":[OSD([sQuery(id+"F56.wireOp",EDGE,"E73.0"),sQuery(id+"F56.wireOp",EDGE,"E75.0")])],"isStart":false});
            cPlane(context, id + "F61", {"entities" : qUnion([Q0, Q1, Q2]), "cplaneType" : CPlaneType.THREE_POINT, "offset" : 25.4 * mm, "width" : 152.4 * mm, "height" : 152.4 * mm});
        }
        {
            var Q0;
            Q0=qCreatedBy(id+"F61.planeOp",FACE);
            var sketch = newSketch(context, id + "F62", { "sketchPlane" : qUnion([Q0])});
            skLineSegment(sketch, "E90", {"start": v(-1005.78, 165.42) * mm, "end": v(-233.74, 215.7) * mm});
            skLineSegment(sketch, "E91", {"start": v(-233.74, 215.7) * mm, "end": v(-233.74, 188.63) * mm});
            skLineSegment(sketch, "E92", {"start": v(-233.74, 188.63) * mm, "end": v(-1008.21, 138.14) * mm});
            skLineSegment(sketch, "E93", {"start": v(-1008.21, 138.14) * mm, "end": v(-1005.78, 165.42) * mm});
            skSolve(sketch);
        }
        {
            var Q0;
            Q0=makeQuery(id+"F62.imprint","IMPRINT",FACE,{"disambiguationData":[TD([[makeQuery(id+"F62.imprint","IMPRINT",EDGE,{"derivedFrom":sQuery(id+"F62.wireOp",EDGE,"E90")}),-1.0]])]});
            extrude(context, id + "F63", {"entities" : qUnion([Q0]), "oppositeDirection" : true, "depth" : 25.4 * mm});
        }
        {
            var Q0;
            Q0=makeQuery(id+"F63.opExtrude","SWEPT_BODY",BODY,{"disambiguationData":[OSD([sQuery(id+"F62.wireOp",EDGE,"E90"),sQuery(id+"F62.wireOp",EDGE,"E91"),sQuery(id+"F62.wireOp",EDGE,"E92"),sQuery(id+"F62.wireOp",EDGE,"E93")])]});
            var Q1;
            Q1=makeQuery(id+"F58.opExtrude","SWEPT_BODY",BODY,{"disambiguationData":[OSD([sQuery(id+"F55.wireOp",EDGE,"E66.0"),sQuery(id+"F55.wireOp",EDGE,"E67.0"),sQuery(id+"F55.wireOp",EDGE,"E68"),sQuery(id+"F55.wireOp",EDGE,"E69.0")])]});
            var Q2;
            Q2=makeQuery(id+"F58.opExtrude","SWEPT_BODY",BODY,{"disambiguationData":[OSD([sQuery(id+"F55.wireOp",EDGE,"E62"),sQuery(id+"F55.wireOp",EDGE,"E63"),sQuery(id+"F55.wireOp",EDGE,"E64"),sQuery(id+"F55.wireOp",EDGE,"E65.0")])]});
            var Q3;
            Q3=makeQuery(id+"F60.opExtrude","SWEPT_BODY",BODY,{"disambiguationData":[OSD([sQuery(id+"F59.wireOp",EDGE,"E86"),sQuery(id+"F59.wireOp",EDGE,"E87.0"),sQuery(id+"F59.wireOp",EDGE,"E88"),sQuery(id+"F59.wireOp",EDGE,"E89")])]});
            var Q4;
            Q4=qCreatedBy(makeId("Front.planeOp"),FACE);
            mirror(context, id + "F64", {"entities" : qUnion([Q0, Q1, Q2, Q3]), "mirrorPlane" : qUnion([Q4])});
        }
        {
            var Q0;
            Q0=makeQuery(id+"F43.opExtrude","CAP_FACE",FACE,{"disambiguationData":[OSD([sQuery(id+"F40.wireOp",EDGE,"E43"),sQuery(id+"F40.wireOp",EDGE,"E44.0"),sQuery(id+"F40.wireOp",EDGE,"E45.0"),sQuery(id+"F40.wireOp",EDGE,"E46"),sQuery(id+"F40.wireOp",EDGE,"E47"),sQuery(id+"F40.wireOp",EDGE,"E48")])],"isStart":true});
            var sketch = newSketch(context, id + "F65", { "sketchPlane" : qUnion([Q0])});
            skLineSegment(sketch, "E94.0", {"start": v(1014.39, 98.32) * mm, "end": v(1014.39, 85.62) * mm});
            skCircle(sketch, "E95", {"center": v(1014.39, 91.97) * mm, "radius": 6.35 * mm});
            skLineSegment(sketch, "E96.0", {"start": v(928.67, 314.04) * mm, "end": v(1025.87, 104.92) * mm});
            skLineSegment(sketch, "E97.0", {"start": v(928.67, 238.72) * mm, "end": v(984.74, 118.09) * mm});
            skLineSegment(sketch, "E98", {"start": v(928.67, 238.72) * mm, "end": v(928.67, 314.04) * mm});
            skLineSegment(sketch, "E99", {"start": v(984.74, 118.09) * mm, "end": v(1025.87, 104.92) * mm});
            skSolve(sketch);
        }
        {
            var Q0;
            Q0=makeQuery(id+"F65.imprint","IMPRINT",FACE,{"disambiguationData":[TD([[makeQuery(id+"F65.imprint","IMPRINT",EDGE,{"derivedFrom":sQuery(id+"F65.wireOp",EDGE,"E96.0")}),-1.0]])]});
            extrude(context, id + "F66", {"entities" : qUnion([Q0]), "oppositeDirection" : true, "depth" : 31.75 * mm});
        }
        {
            var Q0;
            Q0=makeQuery(id+"F66.opExtrude","SWEPT_BODY",BODY,{"disambiguationData":[OSD([sQuery(id+"F65.wireOp",EDGE,"E96.0"),sQuery(id+"F65.wireOp",EDGE,"E97.0"),sQuery(id+"F65.wireOp",EDGE,"E98"),sQuery(id+"F65.wireOp",EDGE,"E99")])]});
            var Q1;
            Q1=qCreatedBy(makeId("Front.planeOp"),FACE);
            mirror(context, id + "F67", {"entities" : qUnion([Q0]), "mirrorPlane" : qUnion([Q1])});
        }
        {
            var Q0;
            Q0=makeQuery(id+"F1.opExtrude","CAP_FACE",FACE,{"disambiguationData":[OSD([sQuery(id+"F0.wireOp",EDGE,"E3"),sQuery(id+"F0.wireOp",EDGE,"E17"),sQuery(id+"F0.wireOp",EDGE,"E19.MirrorCS"),sQuery(id+"F0.wireOp",EDGE,"E20.MirrorCS")])],"isStart":true});
            var sketch = newSketch(context, id + "F68", { "sketchPlane" : qUnion([Q0])});
            skLineSegment(sketch, "E100", {"start": v(-484.38, 162.42) * mm, "end": v(-484.38, -160.96) * mm});
            skLineSegment(sketch, "E101.0", {"start": v(-52.58, 221.26) * mm, "end": v(-52.58, -221.25) * mm});
            skLineSegment(sketch, "E102.0", {"start": v(-33.53, 223.88) * mm, "end": v(-33.53, -223.86) * mm});
            skLineSegment(sketch, "E103", {"start": v(-52.58, -221.25) * mm, "end": v(-33.53, -223.86) * mm});
            skLineSegment(sketch, "E104", {"start": v(-52.58, 221.26) * mm, "end": v(-33.53, 223.88) * mm});
            skSolve(sketch);
        }
        {
            var Q0;
            {var subQ0=sQuery(id+"F68.wireOp",EDGE,"E101.0");Q0=makeQuery(id+"F68.imprint","IMPRINT",FACE,{"disambiguationData":[TD([[makeQuery(id+"F68.imprint","IMPRINT",EDGE,{"derivedFrom":subQ0}),1.0]])]});}
            extrude(context, id + "F69", {"entities" : qUnion([Q0]), "oppositeDirection" : true, "depth" : 19.05 * mm});
        }
    });
